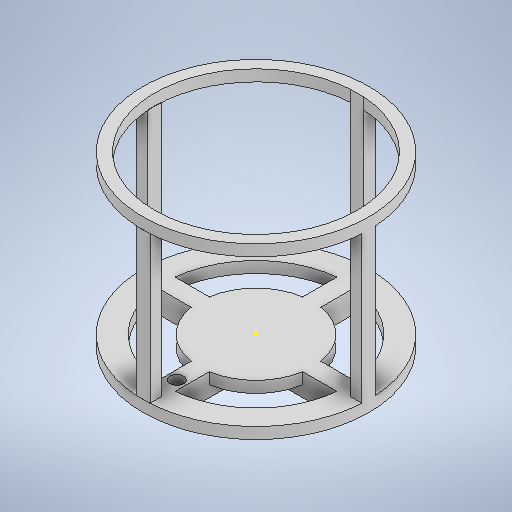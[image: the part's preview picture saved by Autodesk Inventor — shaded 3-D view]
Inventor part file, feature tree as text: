
AUTODESK INVENTOR PART (.ipt)
format: ipt  version: 2025 (Build 290162000, 162)  size: 383,488 bytes
history: native  units: mm
features: sketch x14, extrude x13, other x1
ambient origin geometry x8: Origin, YZ Plane, XZ Plane, XY Plane, X Axis, Y Axis, Z Axis, Center Point
bodies: Body1 (feature_tree)
feature tree (28):
  other  "Bryła1"
  extrude  "Wyciągnięcie proste1"  Depth=100.0mm
  extrude  "Wyciągnięcie proste2"  Depth=80.0mm TaperAngle=0.0deg
  sketch  "Szkic3"
  extrude  "Wyciągnięcie proste3"  Depth=90.0mm
  extrude  "Wyciągnięcie proste4"  Depth=75.0mm TaperAngle=0.0deg
  extrude  "Wyciągnięcie proste5"  Depth=15.0mm
  extrude  "Wyciągnięcie proste6"  Depth=75.0mm TaperAngle=0.0deg
  extrude  "Wyciągnięcie proste7"  Depth=75.0mm TaperAngle=0.0deg
  extrude  "Wyciągnięcie proste8"  Depth=10.0mm TaperAngle=0.0deg
  extrude  "Wyciągnięcie proste9"  Depth=5.0mm TaperAngle=0.0deg
  extrude  "Wyciągnięcie proste10"  Depth=6.0mm
  extrude  "Wyciągnięcie proste11"  Depth=70.0mm TaperAngle=0.0deg
  extrude  "Wyciągnięcie proste12"  Depth=6.0mm
  extrude  "Wyciągnięcie proste13"  Depth=70.0mm TaperAngle=0.0deg
  sketch  "Szkic1"
  sketch  "Szkic2"
  sketch  "Szkic4"
  sketch  "Szkic9"
  sketch  "Szkic10"
  sketch  "Szkic11"
  sketch  "Szkic12"
  sketch  "Szkic13"
  sketch  "Szkic14"
  sketch  "Szkic15"
  sketch  "Szkic16"
  sketch  "Szkic17"
  sketch  "Szkic18"
